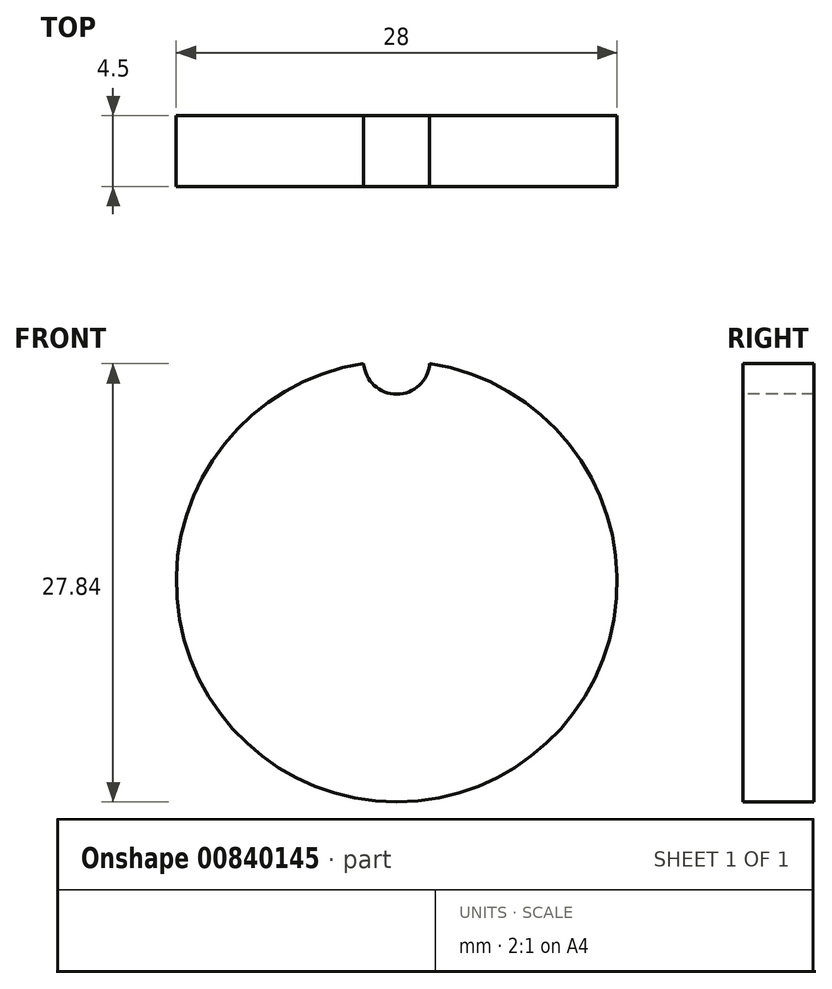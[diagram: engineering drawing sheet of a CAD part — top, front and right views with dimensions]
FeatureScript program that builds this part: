
annotation { "Feature Type Name" : "Feature", "Feature Type Description" : "" }
export const myFeature = defineFeature(function(context is Context, id is Id, definition is map)
    precondition{}
    {
        {
            var Q0;
            Q0=qCreatedBy(makeId("Front.planeOp"),FACE);
            var sketch = newSketch(context, id + "F0", { "sketchPlane" : qUnion([Q0])});
            skCircle(sketch, "E0", {"center": v(0, 0) * mm, "radius": 14 * mm});
            skSolve(sketch);
        }
        {
            var Q0;
            Q0=makeQuery(id+"F0.imprint","IMPRINT",FACE,{"disambiguationData":[TD([[makeQuery(id+"F0.imprint","IMPRINT",EDGE,{"derivedFrom":sQuery(id+"F0.wireOp",EDGE,"E0")}),1.0]])]});
            extrude(context, id + "F1", {"entities" : qUnion([Q0]), "depth" : 4.5 * mm, "offsetDistance" : 25 * mm});
        }
        {
            var Q0;
            Q0=makeQuery(id+"F1.opExtrude","CAP_FACE",FACE,{"disambiguationData":[OSD([sQuery(id+"F0.wireOp",EDGE,"E0")])],"isStart":false});
            var sketch = newSketch(context, id + "F2", { "sketchPlane" : qUnion([Q0])});
            skCircle(sketch, "E1", {"center": v(0, 14) * mm, "radius": 2.1 * mm});
            skSolve(sketch);
        }
        {
            var Q0;
            {var subQ0=sQuery(id+"F2.wireOp",EDGE,"E1");var subQ1=makeQuery(id+"F1.opExtrude","CAP_EDGE",EDGE,{"disambiguationData":[OSD([sQuery(id+"F0.wireOp",EDGE,"E0")])],"isStart":false});var subQ2=makeQuery(id+"F2.imprint","INTERSECT",VERTEX,{"disambiguationData":[OD(0.0)],"derivedFrom":[subQ1,subQ0]});Q0=makeQuery(id+"F2.imprint","IMPRINT",FACE,{"disambiguationData":[TD([[makeQuery(id+"F2.imprint","IMPRINT",EDGE,{"disambiguationData":[TD([[subQ2,-1.0]])],"derivedFrom":subQ0}),1.0]])]});}
            extrude(context, id + "F3", {"entities" : qUnion([Q0]), "operationType" : NewBodyOperationType.REMOVE, "endBound" : BoundingType.THROUGH_ALL, "oppositeDirection" : true, "depth" : 25 * mm, "offsetDistance" : 25 * mm});
        }
    });
